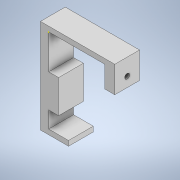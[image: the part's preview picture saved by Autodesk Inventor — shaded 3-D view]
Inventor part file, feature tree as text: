
AUTODESK INVENTOR PART (.ipt)
format: ipt  version: 2021 (Build 250183000, 183)  size: 154,112 bytes
history: native  units: mm
features: extrude x6, sketch x6, other x1
ambient origin geometry x8: Origin, YZ Plane, XZ Plane, XY Plane, X Axis, Y Axis, Z Axis, Center Point
bodies: Body1 (feature_tree)
feature tree (13):
  other  "Sólido1"
  extrude  "Extrusión1"  Depth=5.0mm
  extrude  "Extrusión2"  Depth=12.0mm TaperAngle=0.0deg
  sketch  "Boceto4"  dims[d5=57.0mm d6=0.0mm d7=12.0mm d8=0.0mm]
  extrude  "Extrusión3"  Depth=12.0mm
  extrude  "Extrusión5"  Depth=3.0mm
  extrude  "Extrusión6"  Depth=10.0mm
  extrude  "Extrusión7"  Depth=6.0mm TaperAngle=0.0deg
  sketch  "Boceto3"  dims[d2=3.0mm d3=0.0mm d4=5.0mm]
  sketch  "Boceto5"  dims[d15=12.0mm d16=7.0mm]
  sketch  "Boceto7"  dims[d17=6.0mm d18=3.0mm]
  sketch  "Boceto8"  dims[d19=6.0mm d20=0.0mm d21=10.0mm]
  sketch  "Boceto9"  dims[d22=2.0mm d23=6.0mm d24=0.0mm d25=18.0mm d26=0.0mm]
